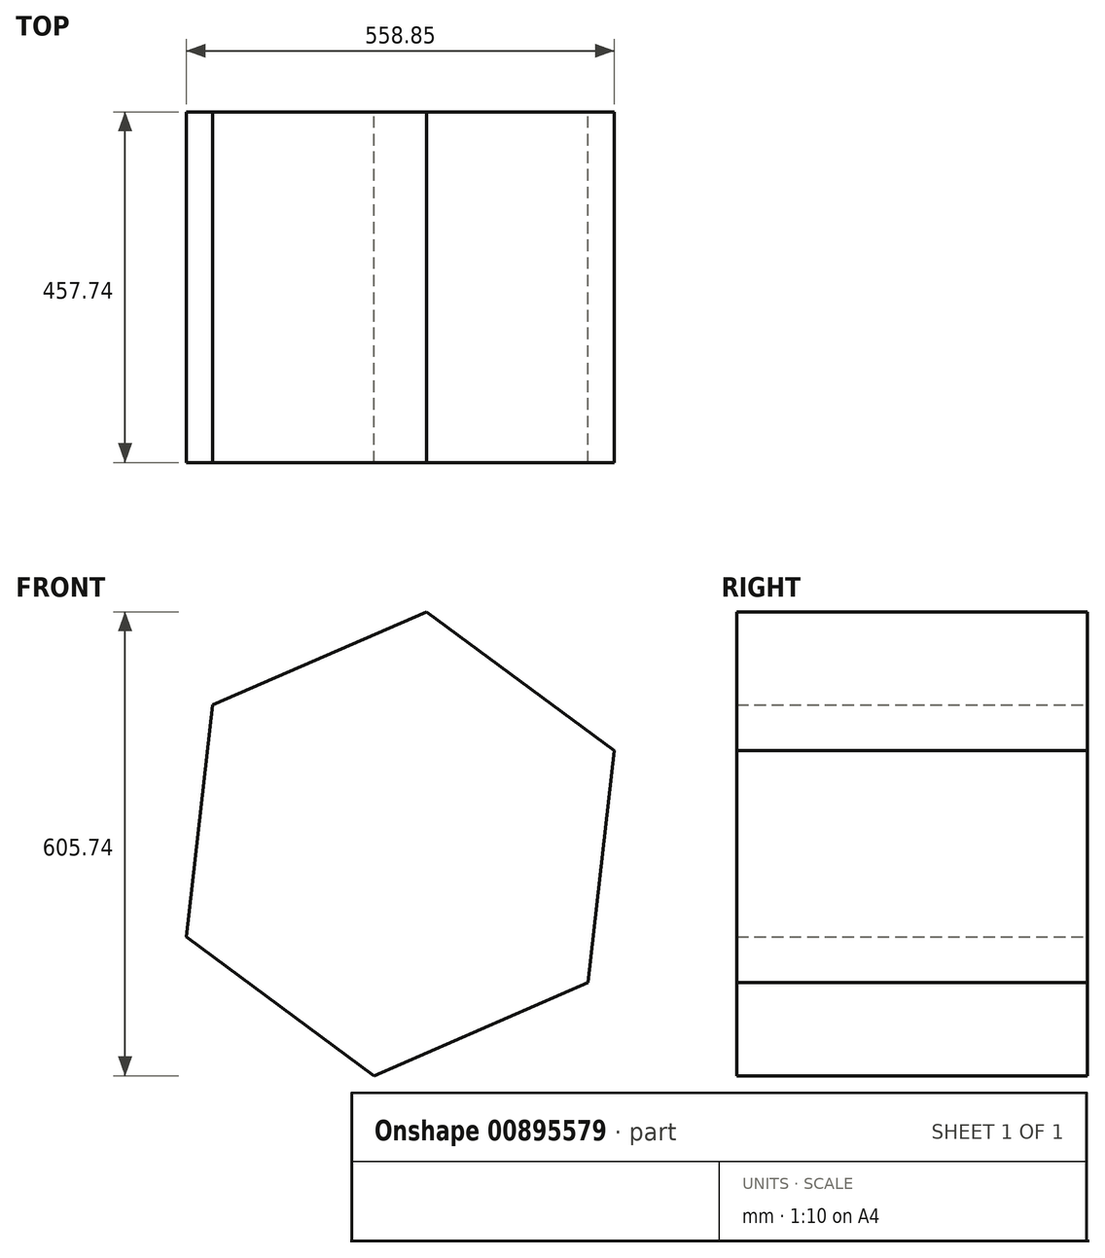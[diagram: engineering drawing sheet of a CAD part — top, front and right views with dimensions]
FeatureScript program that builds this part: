
annotation { "Feature Type Name" : "Feature", "Feature Type Description" : "" }
export const myFeature = defineFeature(function(context is Context, id is Id, definition is map)
    precondition{}
    {
        {
            var Q0;
            Q0=qCreatedBy(makeId("Front.planeOp"),FACE);
            var sketch = newSketch(context, id + "F0", { "sketchPlane" : qUnion([Q0])});
            skLineSegment(sketch, "E0.bottom", {"start": v(-33.5, 44.7) * mm, "end": v(17.4, 44.7) * mm});
            skLineSegment(sketch, "E0.top", {"start": v(-33.5, -17.73) * mm, "end": v(17.4, -17.73) * mm});
            skLineSegment(sketch, "E0.left", {"start": v(-33.5, 44.7) * mm, "end": v(-33.5, -17.73) * mm});
            skLineSegment(sketch, "E0.right", {"start": v(17.4, 44.7) * mm, "end": v(17.4, -17.73) * mm});
            skSolve(sketch);
        }
        {
            var Q0;
            Q0=makeQuery(id+"F0.imprint","IMPRINT",FACE,{"disambiguationData":[TD([[makeQuery(id+"F0.imprint","IMPRINT",EDGE,{"derivedFrom":sQuery(id+"F0.wireOp",EDGE,"E0.bottom")}),-1.0]])]});
            var sketch = newSketch(context, id + "F1", { "sketchPlane" : qUnion([Q0])});
            skSolve(sketch);
        }
        {
            var Q0;
            Q0=qCreatedBy(makeId("Front.planeOp"),FACE);
            var sketch = newSketch(context, id + "F2", { "sketchPlane" : qUnion([Q0])});
            skCircle(sketch, "E1.cCircle", {"center": v(-190.44, 181.1) * mm, "radius": 304.8 * mm, "construction": true});
            skLineSegment(sketch, "E1.0", {"start": v(54.72, 0) * mm, "end": v(-224.7, -121.76) * mm});
            skLineSegment(sketch, "E1.1", {"start": v(-224.7, -121.76) * mm, "end": v(-469.86, 59.35) * mm});
            skLineSegment(sketch, "E1.2", {"start": v(-469.86, 59.35) * mm, "end": v(-435.6, 362.22) * mm});
            skLineSegment(sketch, "E1.3", {"start": v(-435.6, 362.22) * mm, "end": v(-156.17, 483.98) * mm});
            skLineSegment(sketch, "E1.4", {"start": v(-156.17, 483.98) * mm, "end": v(88.99, 302.87) * mm});
            skLineSegment(sketch, "E1.5", {"start": v(88.99, 302.87) * mm, "end": v(54.72, 0) * mm});
            skSolve(sketch);
        }
        {
            var Q0;
            Q0=makeQuery(id+"F2.imprint","IMPRINT",FACE,{"disambiguationData":[TD([[makeQuery(id+"F2.imprint","IMPRINT",EDGE,{"derivedFrom":sQuery(id+"F2.wireOp",EDGE,"E1.0")}),-1.0]])]});
            extrude(context, id + "F3", {"entities" : qUnion([Q0]), "depth" : 457.74 * mm, "offsetDistance" : 25.4 * mm});
        }
    });
